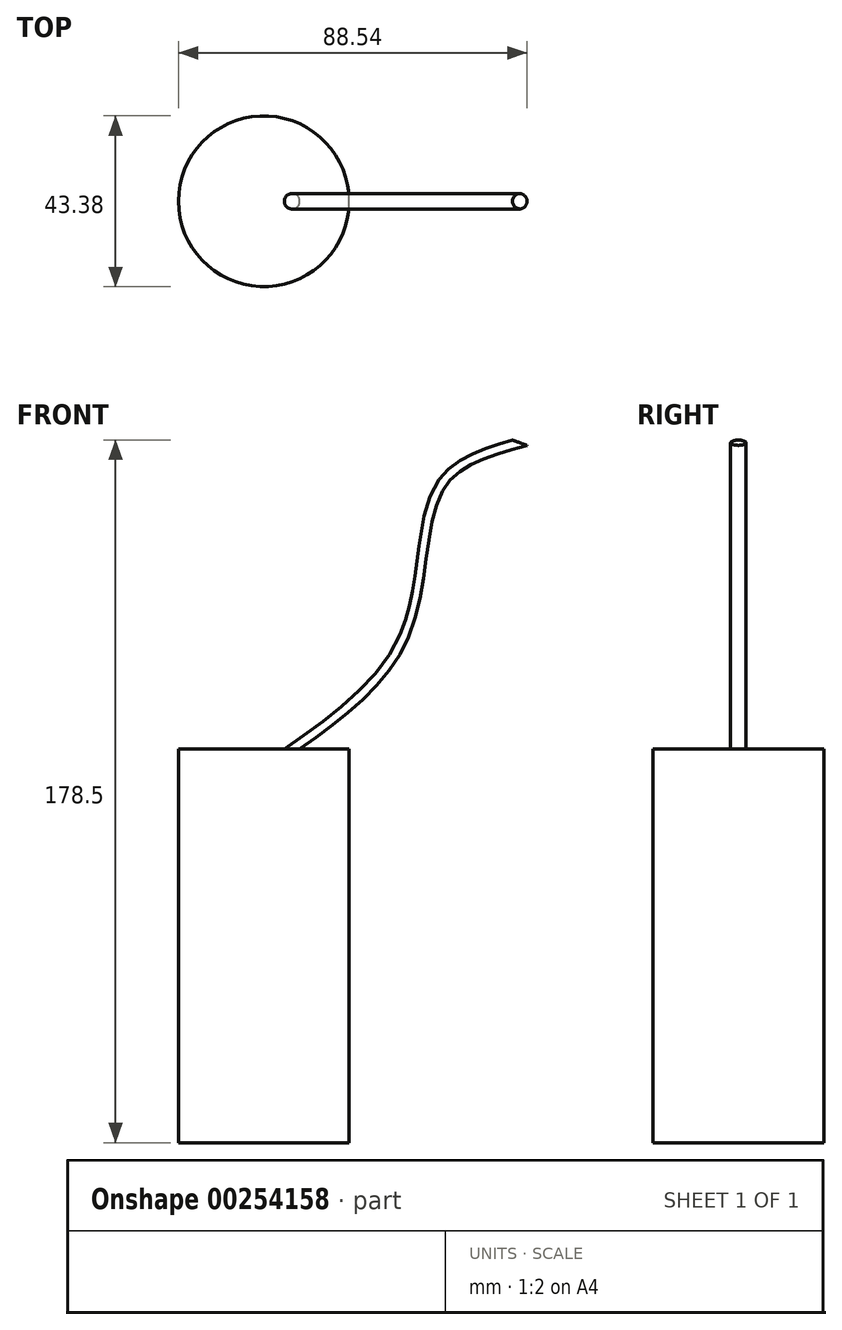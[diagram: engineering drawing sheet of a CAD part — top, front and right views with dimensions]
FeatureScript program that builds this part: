
annotation { "Feature Type Name" : "Feature", "Feature Type Description" : "" }
export const myFeature = defineFeature(function(context is Context, id is Id, definition is map)
    precondition{}
    {
        {
            var Q0;
            Q0=qCreatedBy(makeId("Top.planeOp"),FACE);
            var sketch = newSketch(context, id + "F0", { "sketchPlane" : qUnion([Q0])});
            skCircle(sketch, "E0", {"center": v(-3, 0) * mm, "radius": 21.69 * mm});
            skSolve(sketch);
        }
        {
            var Q0;
            Q0 = qSketchRegion(id + "F0", true);
            extrude(context, id + "F1", {"entities" : qUnion([Q0]), "depth" : 100 * mm});
        }
        {
            var Q0;
            Q0=qCreatedBy(makeId("Front.planeOp"),FACE);
            var sketch = newSketch(context, id + "F2", { "sketchPlane" : qUnion([Q0])});
            skFitSpline(sketch, "E1", {"points": [v(-3.97, 100.43) * mm, v(-16.68, 140.56) * mm, v(-57.2, 170.35) * mm, v(-70.32, 181.48) * mm], "startDerivative": vector(-13.7, 116.58) * mm, "endDerivative": vector(-43.46, 44) * mm});
            skFitSpline(sketch, "E2", {"points": [v(-9.53, 100.43) * mm, v(-38.14, 129.83) * mm, v(-47.67, 151.68) * mm, v(-73.9, 160.42) * mm], "startDerivative": vector(-89.96, 73.17) * mm, "endDerivative": vector(-98.71, 14.9) * mm});
            skFitSpline(sketch, "E3", {"points": [v(-3.97, 100.43) * mm, v(14.3, 135.79) * mm, v(4.77, 169.16) * mm, v(22.25, 184.26) * mm], "startDerivative": vector(77.35, 91.76) * mm, "endDerivative": vector(87.83, 43.04) * mm});
            skFitSpline(sketch, "E4", {"points": [v(3.98, 100.43) * mm, v(32.58, 129.83) * mm, v(41.32, 166.78) * mm, v(61.98, 178.3) * mm], "startDerivative": vector(96.15, 68.47) * mm, "endDerivative": vector(88.8, 24.9) * mm});
            skSolve(sketch);
        }
        {
            var Q0;
            Q0=makeQuery(id+"F1.opExtrude","CAP_FACE",FACE,{"disambiguationData":[OSD([sQuery(id+"F0.wireOp",EDGE,"E0")])],"isStart":false});
            var sketch = newSketch(context, id + "F3", { "sketchPlane" : qUnion([Q0])});
            skCircle(sketch, "E5", {"center": v(4.16, 0) * mm, "radius": 1.95 * mm});
            skSolve(sketch);
        }
        {
            var Q0;
            Q0=makeQuery(id+"F3.imprint","IMPRINT",FACE,{"disambiguationData":[TD([[makeQuery(id+"F3.imprint","IMPRINT",EDGE,{"derivedFrom":sQuery(id+"F3.wireOp",EDGE,"E5")}),1.0]])]});
            var Q1;
            Q1=sQuery(id+"F2.wireOp",EDGE,"E4");
            sweep(context, id + "F4", {"operationType" : NewBodyOperationType.ADD, "profiles" : qUnion([Q0]), "path" : qUnion([Q1])});
        }
    });
